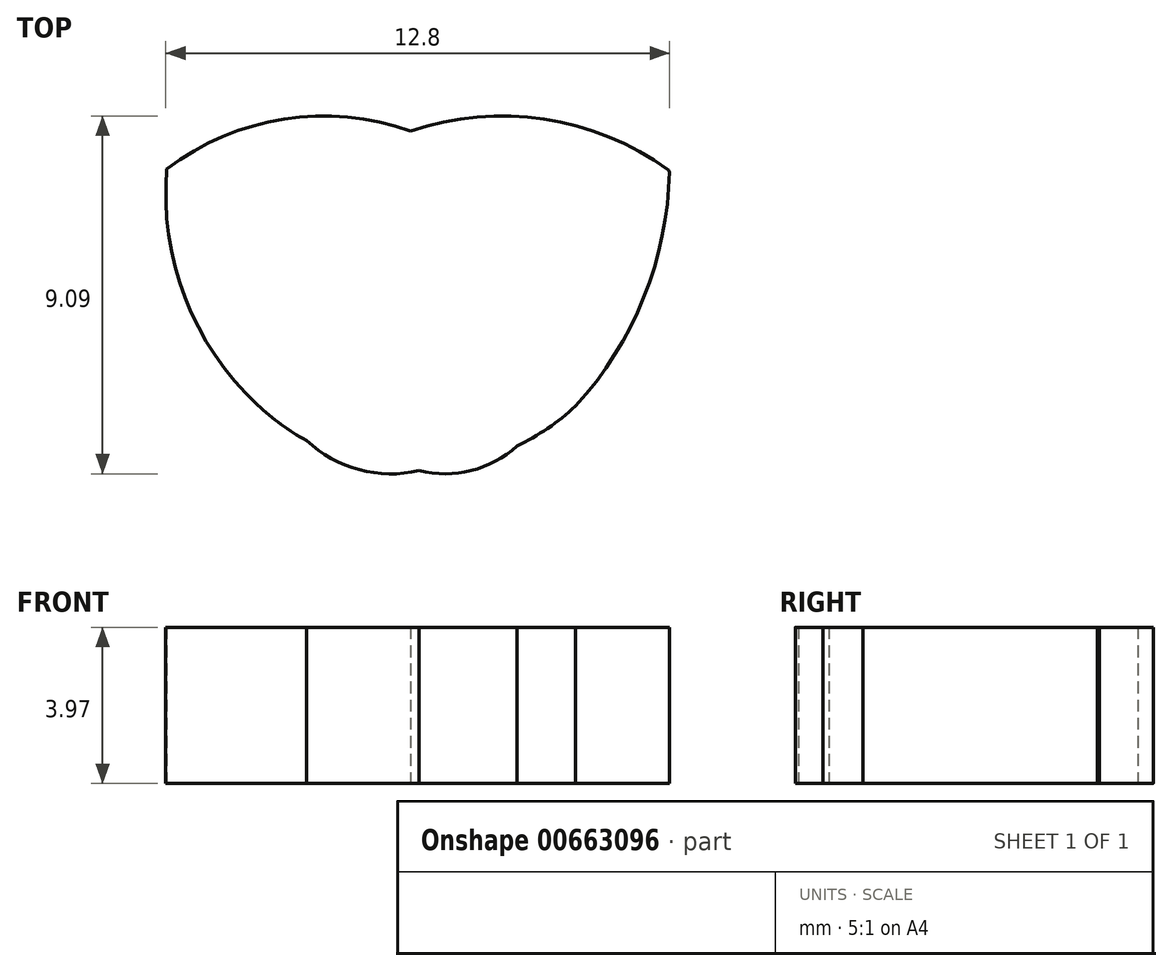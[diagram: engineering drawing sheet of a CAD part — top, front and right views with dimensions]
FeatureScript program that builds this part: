
annotation { "Feature Type Name" : "Feature", "Feature Type Description" : "" }
export const myFeature = defineFeature(function(context is Context, id is Id, definition is map)
    precondition{}
    {
        {
            var Q0;
            Q0=qCreatedBy(makeId("Top.planeOp"),FACE);
            var sketch = newSketch(context, id + "F0", { "sketchPlane" : qUnion([Q0])});
            skPoint(sketch, "E0.center", {"position": v(0, 0) * mm});
            skLineSegment(sketch, "E1", {"start": v(-12.37, 4.64) * mm, "end": v(-12.37, 4.57) * mm});
            skLineSegment(sketch, "E2", {"start": v(7.76, 1.05) * mm, "end": v(7.76, 1.05) * mm});
            skLineSegment(sketch, "E3", {"start": v(8, -1.42) * mm, "end": v(8, -1.42) * mm});
            skLineSegment(sketch, "E4", {"start": v(6.33, 3.65) * mm, "end": v(6.36, 3.6) * mm});
            skArc(sketch, "E5", {"start": v(3.97, -2.35) * mm, "mid": v(5.7, 0.4) * mm, "end": v(6.36, 3.6) * mm});
            skArc(sketch, "E6", {"start": v(-6.41, 3.67) * mm, "mid": v(-5.95, 0.4) * mm, "end": v(-4.1, -2.33) * mm});
            skArc(sketch, "E7", {"start": v(-0.21, 4.63) * mm, "mid": v(-3.44, 4.94) * mm, "end": v(-6.41, 3.67) * mm});
            skArc(sketch, "E8", {"start": v(6.33, 3.65) * mm, "mid": v(3.18, 4.94) * mm, "end": v(-0.21, 4.63) * mm});
            skArc(sketch, "E9", {"start": v(-4.1, -2.33) * mm, "mid": v(-3.51, -2.81) * mm, "end": v(-2.86, -3.23) * mm});
            skArc(sketch, "E10", {"start": v(2.48, -3.37) * mm, "mid": v(3.26, -2.92) * mm, "end": v(3.97, -2.35) * mm});
            skArc(sketch, "E11", {"start": v(-2.86, -3.23) * mm, "mid": v(-1.53, -3.97) * mm, "end": v(0, -4) * mm});
            skArc(sketch, "E12", {"start": v(0, -4) * mm, "mid": v(1.32, -3.99) * mm, "end": v(2.48, -3.37) * mm});
            skSolve(sketch);
        }
        {
            var Q0;
            Q0=makeQuery(id+"F0.imprint","IMPRINT",FACE,{"disambiguationData":[TD([[makeQuery(id+"F0.imprint","IMPRINT",EDGE,{"derivedFrom":sQuery(id+"F0.wireOp",EDGE,"E4")}),-1.0]])]});
            extrude(context, id + "F1", {"entities" : qUnion([Q0]), "depth" : 3.97 * mm, "offsetDistance" : 25.4 * mm});
        }
    });
